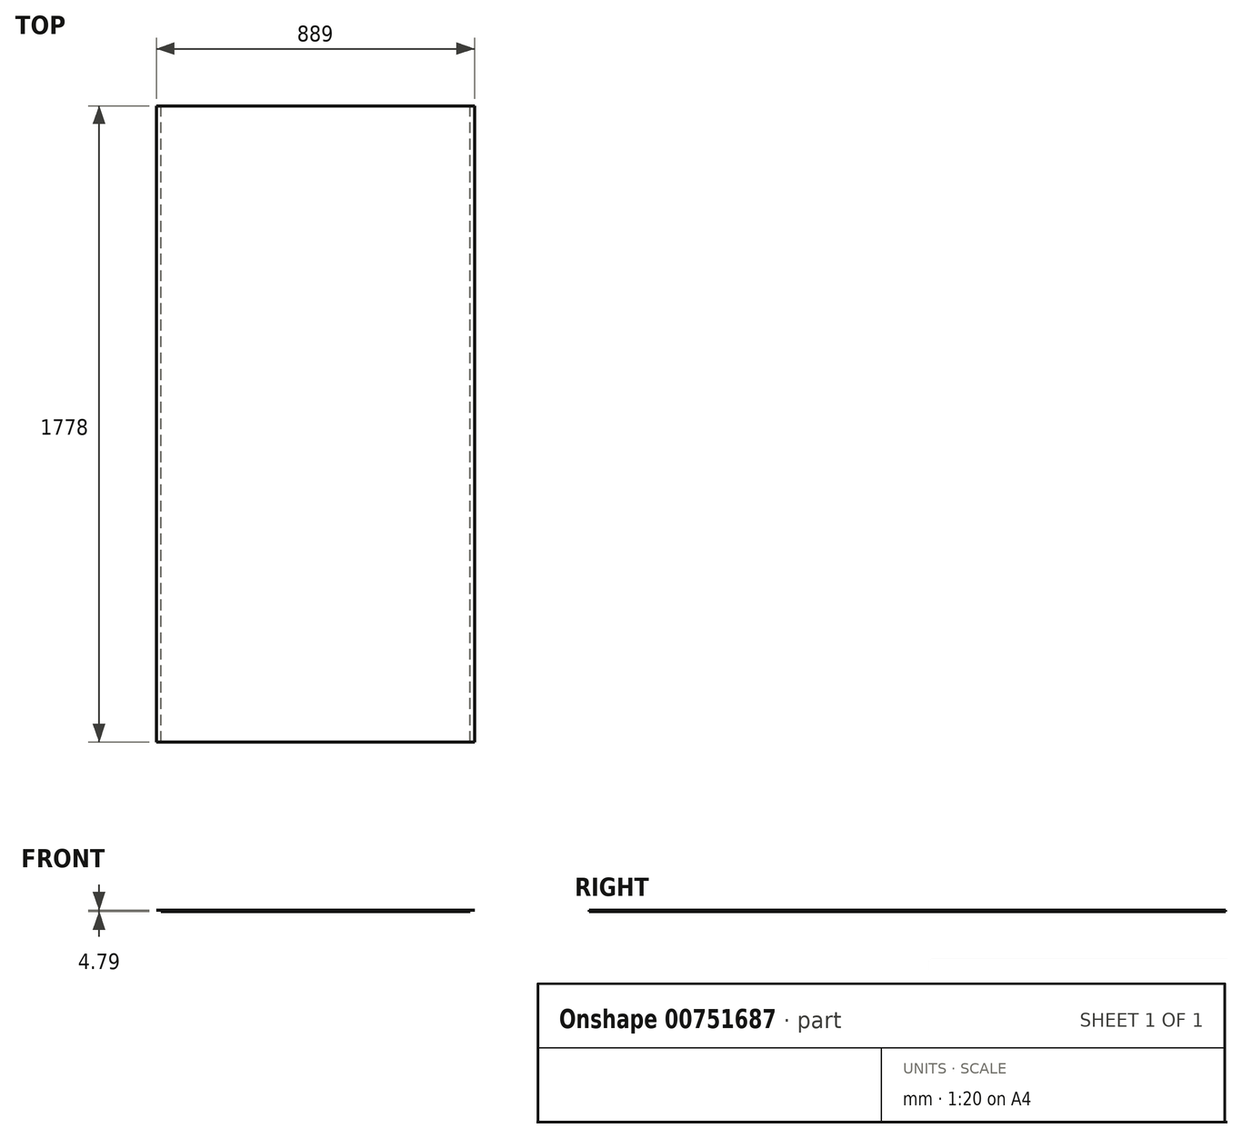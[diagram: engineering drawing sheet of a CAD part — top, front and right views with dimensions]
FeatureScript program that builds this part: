
annotation { "Feature Type Name" : "Feature", "Feature Type Description" : "" }
export const myFeature = defineFeature(function(context is Context, id is Id, definition is map)
    precondition{}
    {
        {
            var Q0;
            Q0=qCreatedBy(makeId("Top.planeOp"),FACE);
            var sketch = newSketch(context, id + "F0", { "sketchPlane" : qUnion([Q0])});
            skLineSegment(sketch, "E0.bottom", {"start": v(-516.8, -887) * mm, "end": v(346.8, -887) * mm});
            skLineSegment(sketch, "E0.top", {"start": v(-516.8, 891) * mm, "end": v(346.8, 891) * mm});
            skLineSegment(sketch, "E0.left", {"start": v(-516.8, -887) * mm, "end": v(-516.8, 891) * mm});
            skLineSegment(sketch, "E0.right", {"start": v(346.8, -887) * mm, "end": v(346.8, 891) * mm});
            skSolve(sketch);
        }
        {
            var Q0;
            Q0=makeQuery(id+"F0.imprint","IMPRINT",FACE,{"disambiguationData":[TD([[makeQuery(id+"F0.imprint","IMPRINT",EDGE,{"derivedFrom":sQuery(id+"F0.wireOp",EDGE,"E0.bottom")}),1.0]])]});
            extrude(context, id + "F1", {"entities" : qUnion([Q0]), "depth" : 3 / 406.4 * mm, "offsetDistance" : 25.4 * mm});
        }
        {
            var Q0;
            Q0=makeQuery(id+"F1.opExtrude","CAP_FACE",FACE,{"disambiguationData":[OSD([sQuery(id+"F0.wireOp",EDGE,"E0.bottom"),sQuery(id+"F0.wireOp",EDGE,"E0.top"),sQuery(id+"F0.wireOp",EDGE,"E0.left"),sQuery(id+"F0.wireOp",EDGE,"E0.right")])],"isStart":false});
            extrude(context, id + "F2", {"entities" : qUnion([Q0]), "operationType" : NewBodyOperationType.ADD, "oppositeDirection" : true, "depth" : 4.76 * mm, "offsetDistance" : 25.4 * mm});
        }
        {
            var Q0;
            Q0=qCreatedBy(makeId("Top.planeOp"),FACE);
            var sketch = newSketch(context, id + "F3", { "sketchPlane" : qUnion([Q0])});
            skLineSegment(sketch, "E1.bottom", {"start": v(-542.2, 891) * mm, "end": v(346.8, 891) * mm});
            skLineSegment(sketch, "E1.top", {"start": v(-542.2, -887) * mm, "end": v(346.8, -887) * mm});
            skLineSegment(sketch, "E1.left", {"start": v(-542.2, 891) * mm, "end": v(-542.2, -887) * mm});
            skLineSegment(sketch, "E1.right", {"start": v(346.8, 891) * mm, "end": v(346.8, -887) * mm});
            skSolve(sketch);
        }
        {
            var Q0;
            Q0 = qSketchRegion(id + "F3", true);
            extrude(context, id + "F4", {"entities" : qUnion([Q0]), "depth" : 7 / 203.2 * mm, "offsetDistance" : 25.4 * mm});
        }
        {
            var Q0;
            Q0=makeQuery(id+"F1.opExtrude","SWEPT_BODY",BODY,{"disambiguationData":[OSD([sQuery(id+"F0.wireOp",EDGE,"E0.bottom"),sQuery(id+"F0.wireOp",EDGE,"E0.top"),sQuery(id+"F0.wireOp",EDGE,"E0.left"),sQuery(id+"F0.wireOp",EDGE,"E0.right")])]});
            transform(context, id + "F5", {"entities" : qUnion([Q0]), "transformType" : TransformType.TRANSLATION_3D, "dx" : -12.7 * mm, "dy" : 0 * mm, "dz" : -3 / 406.4 * mm, "makeCopy" : false});
        }
    });
